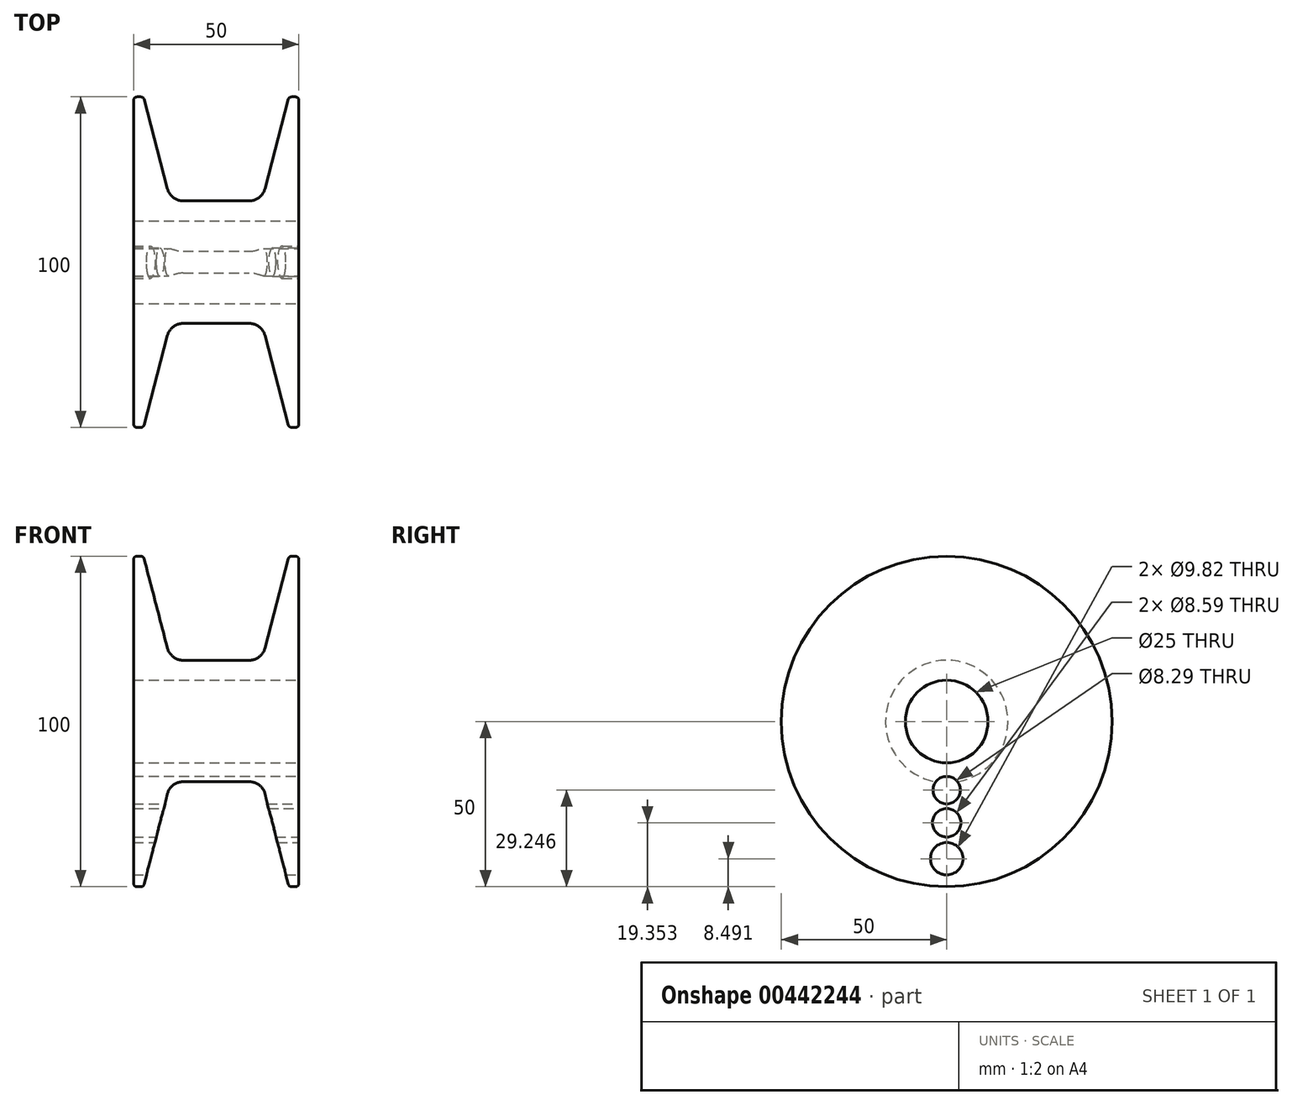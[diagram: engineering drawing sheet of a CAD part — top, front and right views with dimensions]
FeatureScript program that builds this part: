
annotation { "Feature Type Name" : "Feature", "Feature Type Description" : "" }
export const myFeature = defineFeature(function(context is Context, id is Id, definition is map)
    precondition{}
    {
        {
            var Q0;
            Q0=qCreatedBy(makeId("Top.planeOp"),FACE);
            var sketch = newSketch(context, id + "F0", { "sketchPlane" : qUnion([Q0])});
            skPoint(sketch, "E0.middle", {"position": v(0, 0) * mm});
            skLineSegment(sketch, "E1.left", {"start": v(25, 49) * mm, "end": v(25, 5) * mm});
            skLineSegment(sketch, "E1.right", {"start": v(-25, 49) * mm, "end": v(-25, 5) * mm});
            skLineSegment(sketch, "E2.bottom", {"start": v(9.93, 18.52) * mm, "end": v(-9.93, 18.52) * mm});
            skLineSegment(sketch, "E3", {"start": v(-24, 50) * mm, "end": v(-22.77, 50) * mm});
            skLineSegment(sketch, "E4", {"start": v(-21.8, 49.25) * mm, "end": v(-14.77, 22.26) * mm});
            skLineSegment(sketch, "E5", {"start": v(24, 50) * mm, "end": v(22.77, 50) * mm});
            skLineSegment(sketch, "E6", {"start": v(21.8, 49.25) * mm, "end": v(14.77, 22.26) * mm});
            skLineSegment(sketch, "E7", {"start": v(-25, 5) * mm, "end": v(25, 5) * mm});
            skPoint(sketch, "E8.visualSharp", {"position": v(13.8, 18.52) * mm});
            skArc(sketch, "E8.filletArc", {"start": v(9.93, 18.52) * mm, "mid": v(12.99, 19.57) * mm, "end": v(14.77, 22.26) * mm});
            skPoint(sketch, "E9.visualSharp", {"position": v(-13.8, 18.52) * mm});
            skArc(sketch, "E9.filletArc", {"start": v(-14.77, 22.26) * mm, "mid": v(-12.99, 19.57) * mm, "end": v(-9.93, 18.52) * mm});
            skLineSegment(sketch, "E10", {"start": v(-25, 0) * mm, "end": v(25, 0) * mm});
            skPoint(sketch, "E11.visualSharp", {"position": v(-25, 50) * mm});
            skArc(sketch, "E11.filletArc", {"start": v(-24, 50) * mm, "mid": v(-24.7, 49.7) * mm, "end": v(-25, 49) * mm});
            skPoint(sketch, "E12.visualSharp", {"position": v(-22, 50) * mm});
            skArc(sketch, "E12.filletArc", {"start": v(-21.8, 49.25) * mm, "mid": v(-22.16, 49.8) * mm, "end": v(-22.77, 50) * mm});
            skPoint(sketch, "E13.visualSharp", {"position": v(22, 50) * mm});
            skArc(sketch, "E13.filletArc", {"start": v(22.77, 50) * mm, "mid": v(22.16, 49.8) * mm, "end": v(21.8, 49.25) * mm});
            skPoint(sketch, "E14.visualSharp", {"position": v(25, 50) * mm});
            skArc(sketch, "E14.filletArc", {"start": v(25, 49) * mm, "mid": v(24.7, 49.7) * mm, "end": v(24, 50) * mm});
            skSolve(sketch);
        }
        {
            var Q0;
            Q0=makeQuery(id+"F0.imprint","IMPRINT",FACE,{"disambiguationData":[TD([[makeQuery(id+"F0.imprint","IMPRINT",EDGE,{"derivedFrom":sQuery(id+"F0.wireOp",EDGE,"E1.left")}),-1.0]])]});
            var Q1;
            Q1=sQuery(id+"F0.wireOp",EDGE,"E10");
            revolve(context, id + "F1", {"entities" : qUnion([Q0]), "axis" : qUnion([Q1]), "revolveType" : RevolveType.FULL});
        }
        {
            var Q0;
            Q0=makeQuery(id+"F1.opRevolve","SWEPT_FACE",FACE,{"disambiguationData":[OSD([sQuery(id+"F0.wireOp",EDGE,"E1.left")])]});
            var sketch = newSketch(context, id + "F2", { "sketchPlane" : qUnion([Q0])});
            skCircle(sketch, "E15", {"center": v(0, 0) * mm, "radius": 12.5 * mm});
            skSolve(sketch);
        }
        {
            var Q0;
            Q0=makeQuery(id+"F2.imprint","IMPRINT",FACE,{"disambiguationData":[TD([[makeQuery(id+"F2.imprint","IMPRINT",EDGE,{"derivedFrom":sQuery(id+"F2.wireOp",EDGE,"E15")}),1.0]])]});
            extrude(context, id + "F3", {"entities" : qUnion([Q0]), "operationType" : NewBodyOperationType.REMOVE, "endBound" : BoundingType.THROUGH_ALL, "oppositeDirection" : true, "depth" : 25 * mm});
        }
        {
            var Q0;
            Q0=makeQuery(id+"F1.opRevolve","SWEPT_FACE",FACE,{"disambiguationData":[OSD([sQuery(id+"F0.wireOp",EDGE,"E1.left")])]});
            var sketch = newSketch(context, id + "F4", { "sketchPlane" : qUnion([Q0])});
            skCircle(sketch, "E16", {"center": v(0, -20.75) * mm, "radius": 4.15 * mm});
            skCircle(sketch, "E17", {"center": v(0, -30.65) * mm, "radius": 4.3 * mm});
            skCircle(sketch, "E18", {"center": v(0, -41.5) * mm, "radius": 4.91 * mm});
            skSolve(sketch);
        }
        {
            var Q0;
            Q0=makeQuery(id+"F4.imprint","IMPRINT",FACE,{"disambiguationData":[TD([[makeQuery(id+"F4.imprint","IMPRINT",EDGE,{"derivedFrom":sQuery(id+"F4.wireOp",EDGE,"E16")}),1.0]])]});
            var Q1;
            Q1=makeQuery(id+"F4.imprint","IMPRINT",FACE,{"disambiguationData":[TD([[makeQuery(id+"F4.imprint","IMPRINT",EDGE,{"derivedFrom":sQuery(id+"F4.wireOp",EDGE,"E17")}),1.0]])]});
            var Q2;
            Q2=makeQuery(id+"F4.imprint","IMPRINT",FACE,{"disambiguationData":[TD([[makeQuery(id+"F4.imprint","IMPRINT",EDGE,{"derivedFrom":sQuery(id+"F4.wireOp",EDGE,"E18")}),1.0]])]});
            extrude(context, id + "F5", {"entities" : qUnion([Q0, Q1, Q2]), "operationType" : NewBodyOperationType.REMOVE, "endBound" : BoundingType.THROUGH_ALL, "oppositeDirection" : true, "depth" : 25 * mm});
        }
    });
